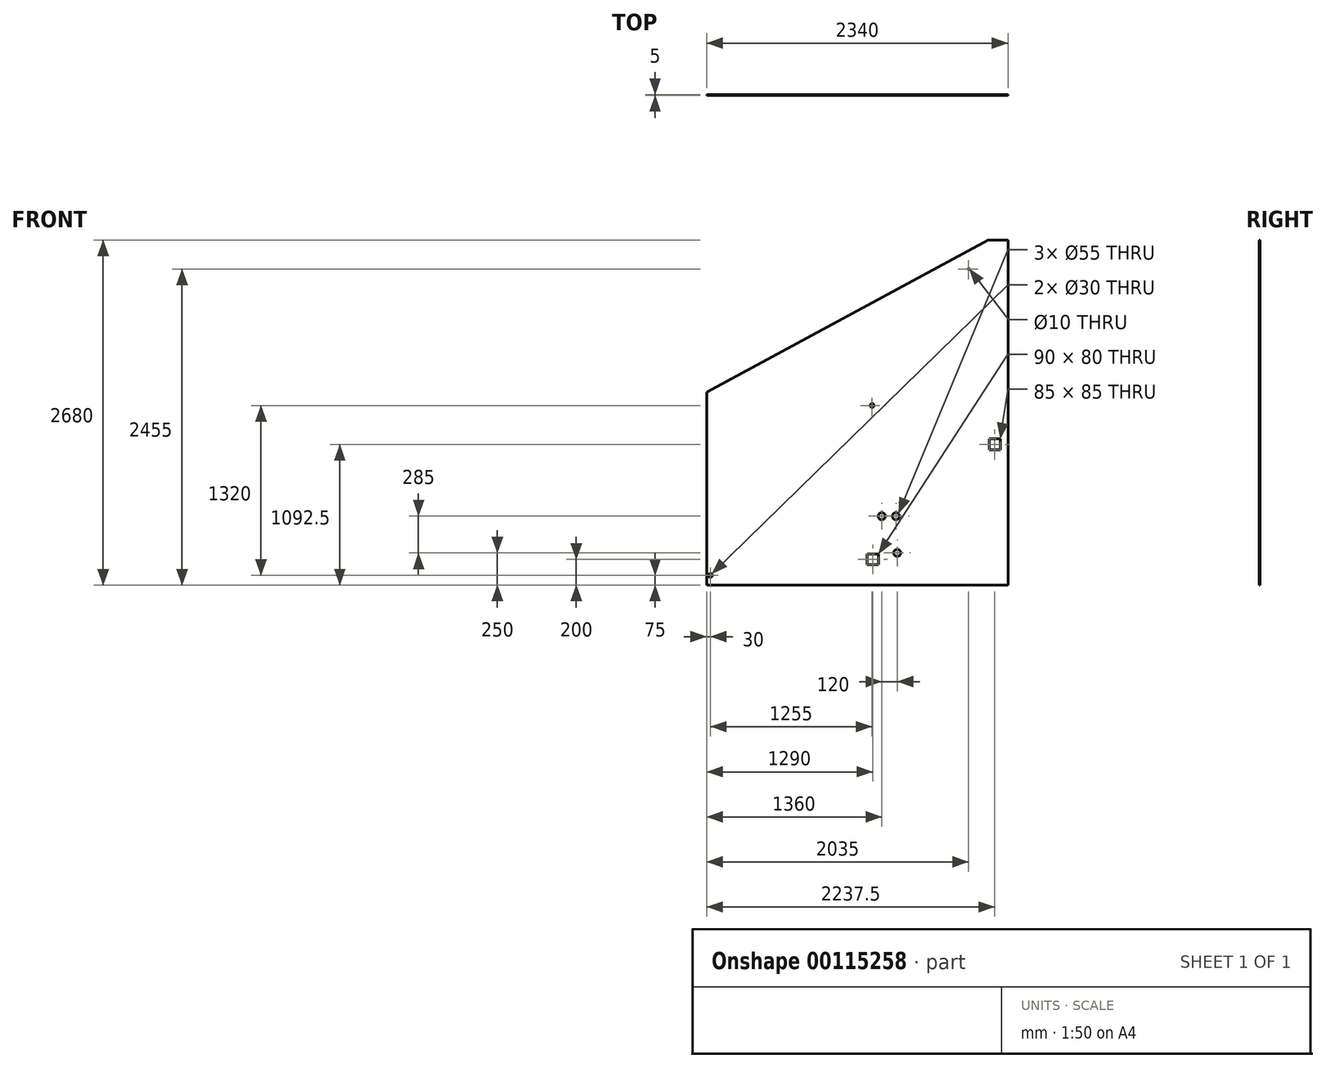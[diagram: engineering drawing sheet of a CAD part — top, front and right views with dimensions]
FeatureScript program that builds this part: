
annotation { "Feature Type Name" : "Feature", "Feature Type Description" : "" }
export const myFeature = defineFeature(function(context is Context, id is Id, definition is map)
    precondition{}
    {
        {
            var Q0;
            Q0=qCreatedBy(makeId("Front.planeOp"),FACE);
            var sketch = newSketch(context, id + "F0", { "sketchPlane" : qUnion([Q0])});
            skLineSegment(sketch, "E0", {"start": v(0, 0) * mm, "end": v(0, 1500) * mm});
            skLineSegment(sketch, "E1", {"start": v(2340, 0) * mm, "end": v(2340, 2680) * mm});
            skLineSegment(sketch, "E2", {"start": v(2340, 2680) * mm, "end": v(2185, 2680) * mm});
            skLineSegment(sketch, "E3", {"start": v(2185, 2680) * mm, "end": v(0, 1500) * mm});
            skLineSegment(sketch, "E4", {"start": v(0, 0) * mm, "end": v(2340, 0) * mm});
            skLineSegment(sketch, "E5.bottom", {"start": v(2195, 1135) * mm, "end": v(2280, 1135) * mm});
            skLineSegment(sketch, "E5.top", {"start": v(2195, 1050) * mm, "end": v(2280, 1050) * mm});
            skLineSegment(sketch, "E5.left", {"start": v(2195, 1135) * mm, "end": v(2195, 1050) * mm});
            skLineSegment(sketch, "E5.right", {"start": v(2280, 1135) * mm, "end": v(2280, 1050) * mm});
            skCircle(sketch, "E6", {"center": v(1285, 1395) * mm, "radius": 15 * mm});
            skCircle(sketch, "E7", {"center": v(1360, 535) * mm, "radius": 27.5 * mm});
            skCircle(sketch, "E8", {"center": v(1470, 535) * mm, "radius": 27.5 * mm});
            skCircle(sketch, "E9", {"center": v(1480, 250) * mm, "radius": 27.5 * mm});
            skLineSegment(sketch, "E10.bottom", {"start": v(1245, 240) * mm, "end": v(1335, 240) * mm});
            skLineSegment(sketch, "E10.top", {"start": v(1245, 160) * mm, "end": v(1335, 160) * mm});
            skLineSegment(sketch, "E10.left", {"start": v(1245, 240) * mm, "end": v(1245, 160) * mm});
            skLineSegment(sketch, "E10.right", {"start": v(1335, 240) * mm, "end": v(1335, 160) * mm});
            skCircle(sketch, "E11", {"center": v(30, 75) * mm, "radius": 15 * mm});
            skCircle(sketch, "E12", {"center": v(2035, 2455) * mm, "radius": 5 * mm});
            skSolve(sketch);
        }
        {
            var Q0;
            Q0=makeQuery(id+"F0.imprint","IMPRINT",FACE,{"disambiguationData":[TD([[makeQuery(id+"F0.imprint","IMPRINT",EDGE,{"derivedFrom":sQuery(id+"F0.wireOp",EDGE,"E0")}),-1.0]])]});
            extrude(context, id + "F1", {"entities" : qUnion([Q0]), "depth" : 5 * mm});
        }
    });
